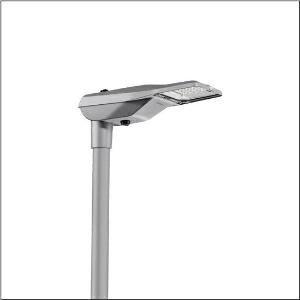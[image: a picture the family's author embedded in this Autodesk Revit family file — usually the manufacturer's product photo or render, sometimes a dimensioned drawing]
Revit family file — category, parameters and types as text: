
# Revit family: streetlight_sl_21_micro___pl52_5xe1h33t08db_704d
name_source: partatom
category: Lighting Fixtures
units: mm (PartAtom-declared; Revit-internal decimal feet)

## family parameters
Cut with Voids When Loaded = No
Host = Face
Light Source = No
Part Type = Normal
Room Calculation Point = No
Round Connector Dimension = Use Diameter
Shared = No

## types (1)
- --- (1 x LED, 5020 lm, 39.1 W, 3000K)
    Apparent Load = 39 VA
    CIE Flux Codes = 27 59 98 100 100
    Color Rendering = 70
    Color Temperature = 3000K
    Default Elevation = 1800 mm
    Description = Streetlight SL 21 micro, mast luminaire, primary light control with lens, of PMMA, primary optical cover: cover, of toughened safety glass, transparent, light distribution: PL52, light emission: direct distribution, primary light characteristic: asymmetric, installation type: side-entry, post-top, LED, High Power LED, rated luminous flux: 5.020lm, luminous efficacy: 128lm/W, light colour: 730, colour temperature: 3000K, control: flexible luminous flux parameterisation, time-dependent luminous flux control, constant luminous flux control, overheat protection, pre-setting: logarithmic dimming characteristic, mains connection: 220..240V, AC, 50/60Hz, start of lifetime: 39W, end of service life: 41W, reduction: 18W, luminaire housing, of diecast aluminium, powder-coated, Siteco® metallic grey (DB 702S), corrosivity category C5 mid according to DIN EN ISO 12944, please order mast flange separately, inclination adjustable: 0°, 5°, 10°, 15°, sealing non-destructively replaceable, multi-level sealing system, length: 528mm, width: 235mm, height: 110mm, mast flange for spigot size: 42mm (side-entry): 5XC10008XM4, 60/48mm (side-entry/post-top): 5XC10108XM2, 76/60mm (side-entry/post-top): 5XC10108XM1, Smart Interface below and above, protection rating (complete): IP66, insulation class (complete): insulation class II (safety insulation), certification: CE, ENEC, ENEC+, VDE, impact resistance: IK09, permissible operating ambient temperature for outdoor applications: -40..+50°C, standard-compliant lighting for roads and squares, packaging unit: 1 piece

Light Distribution: PL52
    Height = 110 mm
    Lamp = 1 x LED
    Lamp Light Flux = 5020 lm
    Lamp Power = 39.1 W
    Lamp count = 1
    Length = 528 mm
    Luminous efficacy = 128 lm/W
    Manufacturer = Siteco
    ModVariant = No
    Model = 5XE1H33T08DB
    Number of Poles = 1
    OnlyDefault = Yes
    Power Factor = 1
    Product Name = Streetlight SL 21 micro | PL52
    Product group = mast luminaire | pylon top
    ProductGroupID = 6100
    Protection Class = Protection class II
    Protection Degree = IP 66
    RLX_Detail_Level = 1
    RLX_Emergency_Light_Flux = 0 lm
    RLX_Emergency_Type = 0
    RLX_Emergency_Type_DB = No
    RlxData = <blob elided: 107669 chars, md5=82396aaf>
    Socket = socket
    Standby Power = 0 W
    System Light Flux = 5020 lm
    System Power = 39 W
    Type Comments = factory setting: luminous flux: 100 % | dim-lin: 254 | 765 mA
    Type Image = l_1007239.jpg
    URL = http://relux.com
    VarID = @adj_126545
    Voltage = 0 V
    Weight = 0.00 kg
    Width = 235 mm

## geometry (parser evidence)
native form markers: Blend x4, Sweep x11
no freeform markers — native parametric forms only
